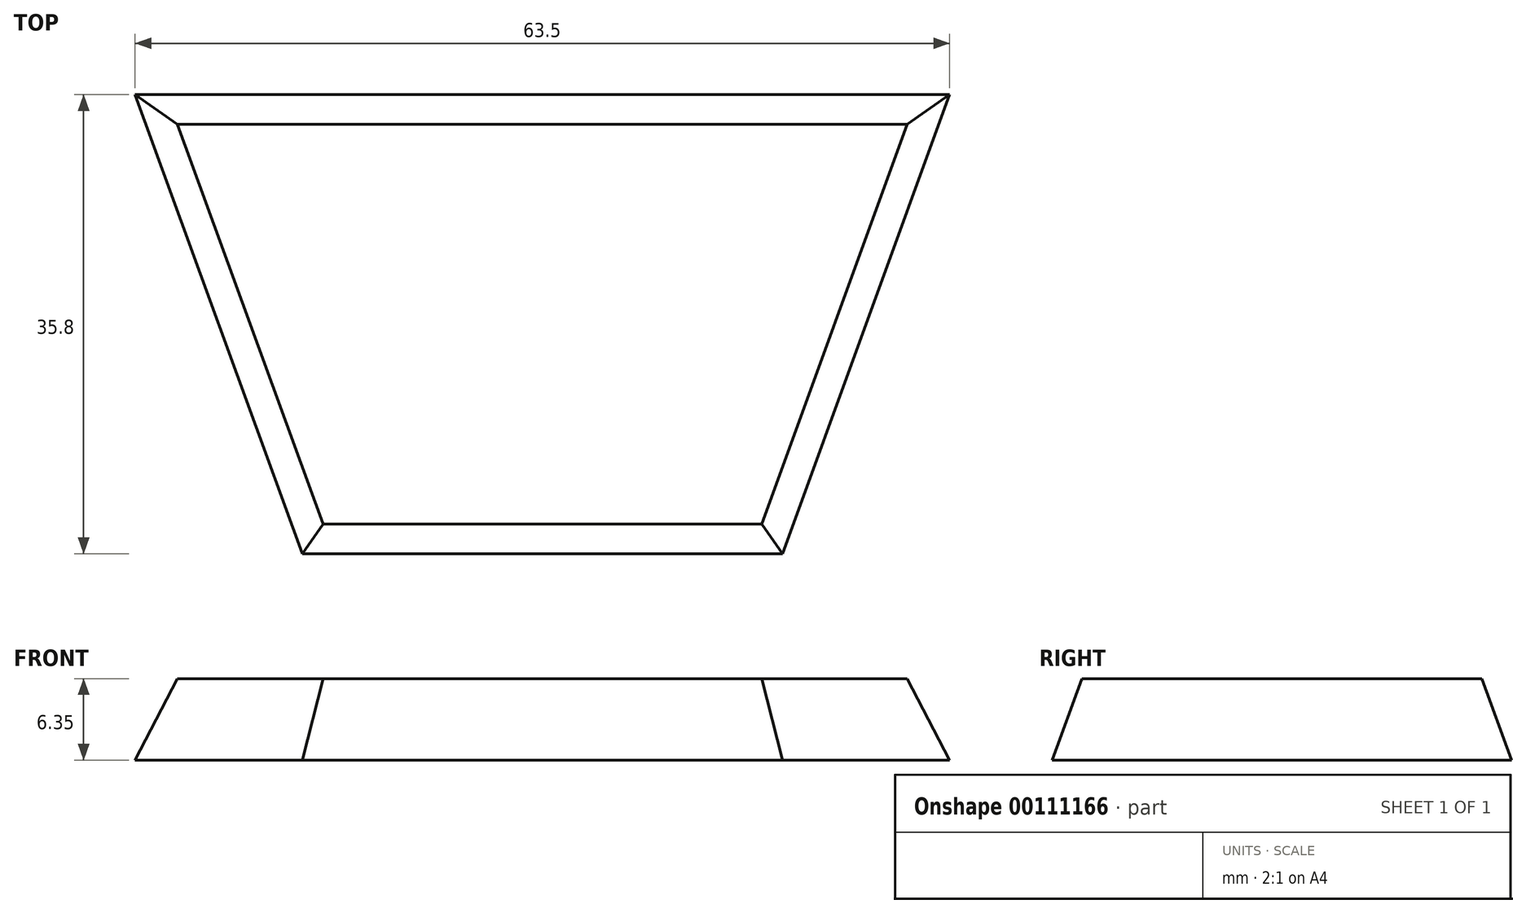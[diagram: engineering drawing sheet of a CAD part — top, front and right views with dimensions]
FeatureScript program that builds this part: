
annotation { "Feature Type Name" : "Feature", "Feature Type Description" : "" }
export const myFeature = defineFeature(function(context is Context, id is Id, definition is map)
    precondition{}
    {
        {
            var Q0;
            Q0=qCreatedBy(makeId("Top.planeOp"),FACE);
            var sketch = newSketch(context, id + "F0", { "sketchPlane" : qUnion([Q0])});
            skLineSegment(sketch, "E0", {"start": v(-32.24, 24.28) * mm, "end": v(31.26, 24.28) * mm});
            skLineSegment(sketch, "E1", {"start": v(-32.24, 24.28) * mm, "end": v(-19.2, -11.52) * mm});
            skLineSegment(sketch, "E2", {"start": v(-19.2, -11.52) * mm, "end": v(18.23, -11.52) * mm});
            skLineSegment(sketch, "E3", {"start": v(18.23, -11.52) * mm, "end": v(31.26, 24.28) * mm});
            skSolve(sketch);
        }
        {
            var Q0;
            Q0=makeQuery(id+"F0.imprint","IMPRINT",FACE,{"disambiguationData":[TD([[makeQuery(id+"F0.imprint","IMPRINT",EDGE,{"derivedFrom":sQuery(id+"F0.wireOp",EDGE,"E0")}),-1.0]])]});
            extrude(context, id + "F1", {"entities" : qUnion([Q0]), "depth" : 6.35 * mm, "hasDraft" : true, "draftAngle" : 20 * degree, "draftPullDirection" : true});
        }
    });
